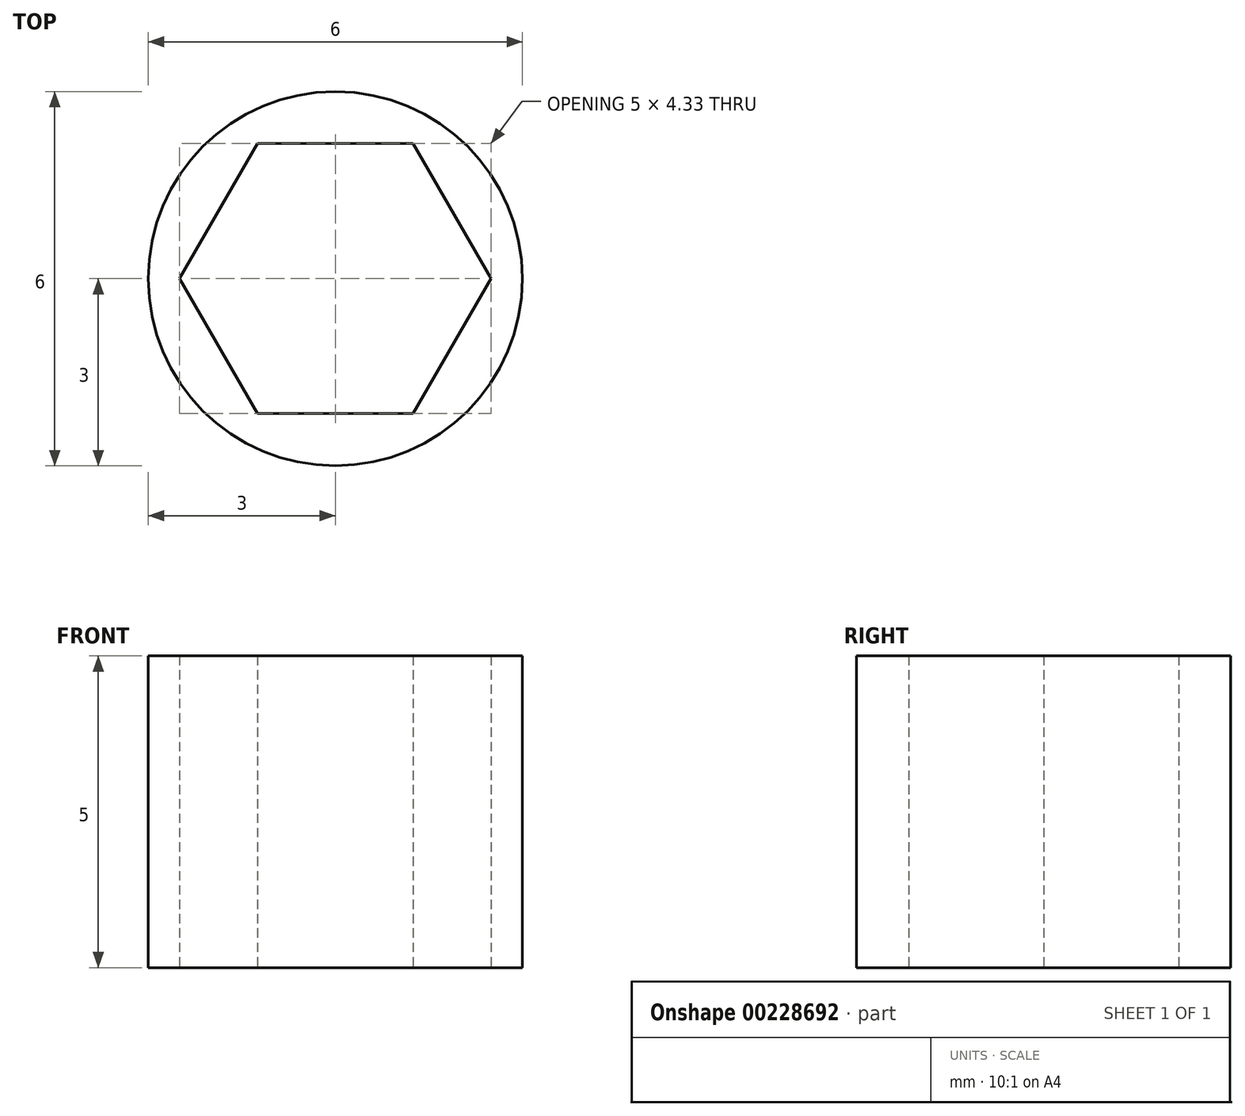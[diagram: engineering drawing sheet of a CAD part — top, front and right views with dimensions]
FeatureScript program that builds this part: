
annotation { "Feature Type Name" : "Feature", "Feature Type Description" : "" }
export const myFeature = defineFeature(function(context is Context, id is Id, definition is map)
    precondition{}
    {
        {
            var Q0;
            Q0=qCreatedBy(makeId("Top.planeOp"),FACE);
            var sketch = newSketch(context, id + "F0", { "sketchPlane" : qUnion([Q0])});
            skCircle(sketch, "E0", {"center": v(0, 0) * mm, "radius": 2.5 * mm, "construction": true});
            skCircle(sketch, "E1", {"center": v(0, 0) * mm, "radius": 3 * mm});
            skLineSegment(sketch, "E2.0", {"start": v(2.5, 0) * mm, "end": v(1.25, -2.17) * mm});
            skLineSegment(sketch, "E2.1", {"start": v(1.25, -2.17) * mm, "end": v(-1.25, -2.17) * mm});
            skLineSegment(sketch, "E2.2", {"start": v(-1.25, -2.17) * mm, "end": v(-2.5, 0) * mm});
            skLineSegment(sketch, "E2.3", {"start": v(-2.5, 0) * mm, "end": v(-1.25, 2.17) * mm});
            skLineSegment(sketch, "E2.4", {"start": v(-1.25, 2.17) * mm, "end": v(1.25, 2.17) * mm});
            skLineSegment(sketch, "E2.5", {"start": v(1.25, 2.17) * mm, "end": v(2.5, 0) * mm});
            skSolve(sketch);
        }
        {
            var Q0;
            Q0=makeQuery(id+"F0.imprint","IMPRINT",FACE,{"disambiguationData":[TD([[makeQuery(id+"F0.imprint","IMPRINT",EDGE,{"derivedFrom":sQuery(id+"F0.wireOp",EDGE,"E1")}),1.0]])]});
            extrude(context, id + "F1", {"entities" : qUnion([Q0]), "depth" : 5 * mm});
        }
    });
